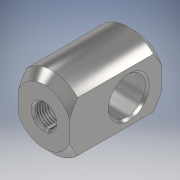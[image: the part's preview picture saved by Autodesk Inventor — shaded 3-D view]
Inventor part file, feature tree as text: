
AUTODESK INVENTOR PART (.ipt)
format: ipt  version: 2021 (Build 250183000, 183)  size: 159,744 bytes
history: native  units: mm
features: sketch x4, extrude x3, chamfer x3, pattern_circular x1, hole x1
ambient origin geometry x8: Origin, YZ Plane, XZ Plane, XY Plane, X Axis, Y Axis, Z Axis, Center Point
bodies: Solid1 (feature_tree)
feature tree (12):
  extrude  "Extrusion1"  Depth=45.0mm TaperAngle=0.0deg
  extrude  "Extrusion2"  TaperAngle=0.0deg  [1 undecoded]
  pattern_circular  "Circular Pattern1"  Count=2 Angle=360.0deg
  extrude  "Extrusion3"  Depth=16.0mm
  hole  "Hole1"  [1 undecoded]
  chamfer  "Chamfer1"  Distance=1.0mm Angle=45.0deg
  chamfer  "Chamfer2"  Distance=1.0mm Angle=45.0deg
  chamfer  "Chamfer3"  [1 undecoded]
  sketch  "Sketch1"  dims[d0=35.0mm d1=45.0mm d2=0.0mm]
  sketch  "Sketch2"  dims[d3=12.5mm d4=0.0mm d5=0.0mm d6=20.0mm d7=360.0deg]
  sketch  "Sketch3"  dims[d9=18.0mm d10=16.0mm]
  sketch  "Sketch4"  dims[d11=0.0mm d12=0.0mm d13=10.647mm d14=20.0mm d15=4.0mm d16=2.0mm d17=90.0deg d18=25.0mm d19=20.594885mm d20=4.0mm d21=2.0mm d22=45.0deg d23=1.0mm d24=2.0mm d25=45.0deg d26=1.0mm d27=2.0mm d28=45.0deg]
note: 3 required parameter values undecoded (feature->parameter linkage not recoverable at this tier; creation-order binding heuristic only, values carry confidence <= 0.55)
